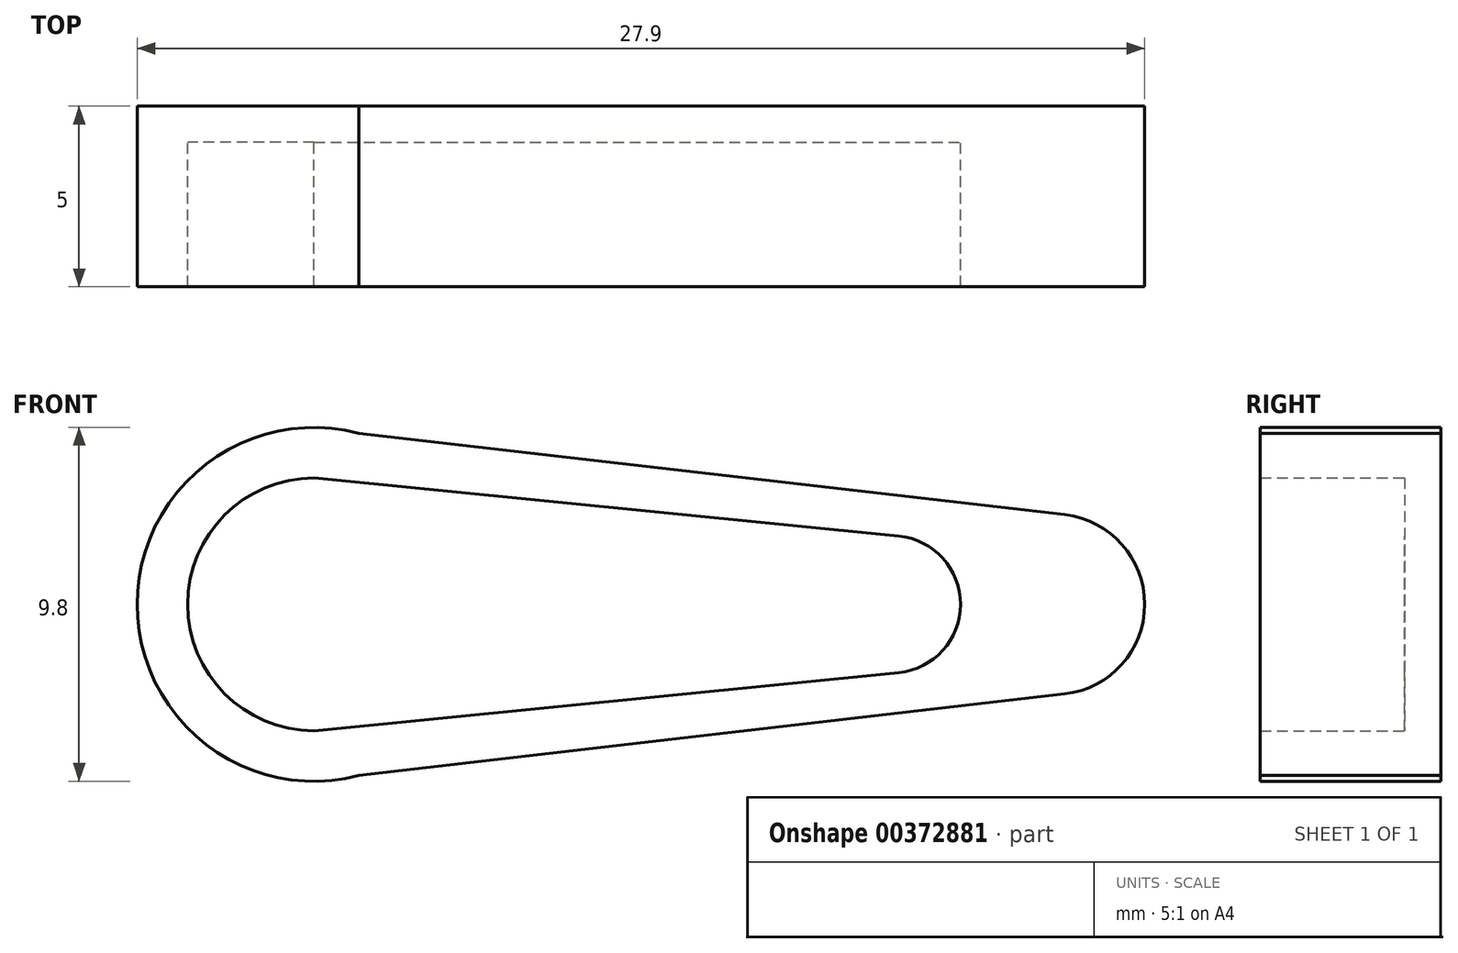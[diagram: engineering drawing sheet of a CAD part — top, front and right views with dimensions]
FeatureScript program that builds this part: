
annotation { "Feature Type Name" : "Feature", "Feature Type Description" : "" }
export const myFeature = defineFeature(function(context is Context, id is Id, definition is map)
    precondition{}
    {
        {
            var Q0;
            Q0=qCreatedBy(makeId("Front.planeOp"),FACE);
            var sketch = newSketch(context, id + "F0", { "sketchPlane" : qUnion([Q0])});
            skArc(sketch, "E0", {"start": v(0, 3.5) * mm, "mid": v(-3.5, 0) * mm, "end": v(0, -3.5) * mm});
            skLineSegment(sketch, "E1", {"start": v(0, 0) * mm, "end": v(16, 0) * mm, "construction": true});
            skArc(sketch, "E2", {"start": v(16.19, -1.9) * mm, "mid": v(17.9, 0) * mm, "end": v(16.19, 1.9) * mm});
            skLineSegment(sketch, "E3", {"start": v(0, 3.5) * mm, "end": v(16.19, 1.9) * mm});
            skLineSegment(sketch, "E4", {"start": v(0, -3.5) * mm, "end": v(16.19, -1.9) * mm});
            skArc(sketch, "E5", {"start": v(20.79, -2.48) * mm, "mid": v(23, 0) * mm, "end": v(20.79, 2.48) * mm});
            skArc(sketch, "E6", {"start": v(1.23, 4.74) * mm, "mid": v(-4.9, 0) * mm, "end": v(1.23, -4.74) * mm});
            skLineSegment(sketch, "E7", {"start": v(1.23, 4.74) * mm, "end": v(20.79, 2.48) * mm});
            skLineSegment(sketch, "E8", {"start": v(1.23, -4.74) * mm, "end": v(20.79, -2.48) * mm});
            skSolve(sketch);
        }
        {
            var Q0;
            Q0=makeQuery(id+"F0.imprint","IMPRINT",FACE,{"disambiguationData":[TD([[makeQuery(id+"F0.imprint","IMPRINT",EDGE,{"derivedFrom":sQuery(id+"F0.wireOp",EDGE,"E0")}),-1.0]])]});
            var Q1;
            {var subQ0=sQuery(id+"F0.wireOp",EDGE,"E5");var subQ1=makeQuery(id+"F0.imprint","INTERSECT",VERTEX,{"derivedFrom":[subQ0,sQuery(id+"F0.wireOp",EDGE,"B0DNySFA-kTdr-VNrI-f1jD-I2K1M4yv6boT")]});Q1=makeQuery(id+"F0.imprint","IMPRINT",FACE,{"disambiguationData":[TD([[makeQuery(id+"F0.imprint","IMPRINT",EDGE,{"disambiguationData":[TD([[subQ1,-1.0]])],"derivedFrom":subQ0}),1.0]])]});}
            extrude(context, id + "F1", {"entities" : qUnion([Q0, Q1]), "depth" : 5 * mm, "offsetDistance" : 25 * mm});
        }
        {
            var Q0;
            Q0=makeQuery(id+"F0.imprint","IMPRINT",FACE,{"disambiguationData":[TD([[makeQuery(id+"F0.imprint","IMPRINT",EDGE,{"derivedFrom":sQuery(id+"F0.wireOp",EDGE,"E0")}),-1.0]])]});
            var Q1;
            {var subQ0=sQuery(id+"F0.wireOp",EDGE,"E5");var subQ1=makeQuery(id+"F0.imprint","INTERSECT",VERTEX,{"derivedFrom":[subQ0,sQuery(id+"F0.wireOp",EDGE,"B0DNySFA-kTdr-VNrI-f1jD-I2K1M4yv6boT")]});Q1=makeQuery(id+"F0.imprint","IMPRINT",FACE,{"disambiguationData":[TD([[makeQuery(id+"F0.imprint","IMPRINT",EDGE,{"disambiguationData":[TD([[subQ1,-1.0]])],"derivedFrom":subQ0}),1.0]])]});}
            var Q2;
            Q2=makeQuery(id+"F0.imprint","IMPRINT",FACE,{"disambiguationData":[TD([[makeQuery(id+"F0.imprint","IMPRINT",EDGE,{"derivedFrom":sQuery(id+"F0.wireOp",EDGE,"E0")}),1.0]])]});
            extrude(context, id + "F2", {"entities" : qUnion([Q0, Q1, Q2]), "operationType" : NewBodyOperationType.ADD, "depth" : 1 * mm, "offsetDistance" : 25 * mm});
        }
    });
